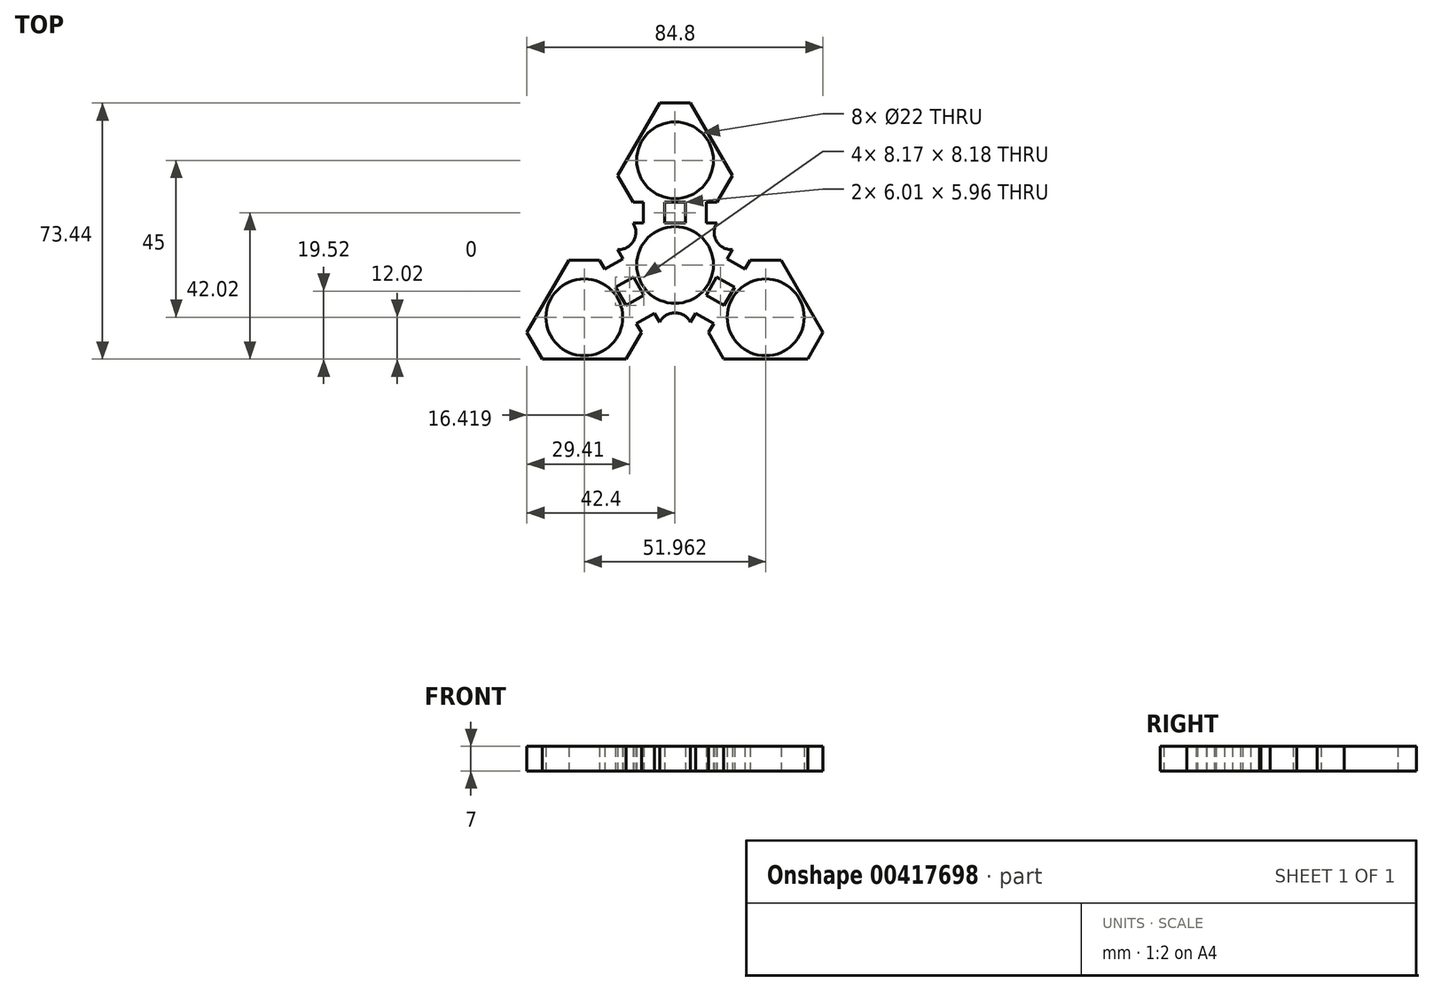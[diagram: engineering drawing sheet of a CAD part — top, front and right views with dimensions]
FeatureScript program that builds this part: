
annotation { "Feature Type Name" : "Feature", "Feature Type Description" : "" }
export const myFeature = defineFeature(function(context is Context, id is Id, definition is map)
    precondition{}
    {
        {
            var Q0;
            Q0=qCreatedBy(makeId("Top.planeOp"),FACE);
            var sketch = newSketch(context, id + "F0", { "sketchPlane" : qUnion([Q0])});
            skCircle(sketch, "E0", {"center": v(0, 0) * mm, "radius": 11 * mm});
            skLineSegment(sketch, "E1", {"start": v(0, 0) * mm, "end": v(0, 30) * mm});
            skCircle(sketch, "E2", {"center": v(0, 30) * mm, "radius": 11 * mm});
            skLineSegment(sketch, "E3.1.0", {"start": v(0, 0) * mm, "end": v(-25.98, -15) * mm});
            skCircle(sketch, "E3.1.1", {"center": v(-25.98, -15) * mm, "radius": 11 * mm});
            skLineSegment(sketch, "E3.2.0", {"start": v(0, 0) * mm, "end": v(25.98, -15) * mm});
            skCircle(sketch, "E3.2.1", {"center": v(25.98, -15) * mm, "radius": 11 * mm});
            skLineSegment(sketch, "E4", {"start": v(12.02, 12.02) * mm, "end": v(6.01, 12.02) * mm});
            skLineSegment(sketch, "E5.1.0", {"start": v(-16.42, 4.4) * mm, "end": v(-4.4, -16.42) * mm});
            skLineSegment(sketch, "E5.2.0", {"start": v(4.4, -16.42) * mm, "end": v(16.42, 4.4) * mm});
            skPoint(sketch, "E6", {"position": v(0, 15) * mm});
            skLineSegment(sketch, "E7.MirrorCS", {"start": v(12.02, 17.98) * mm, "end": v(0, 17.98) * mm});
            skLineSegment(sketch, "E8.MirrorCS", {"start": v(16.42, 25.6) * mm, "end": v(12.02, 17.98) * mm});
            skLineSegment(sketch, "E9.MirrorCS", {"start": v(4.4, 46.42) * mm, "end": v(16.42, 25.6) * mm});
            skLineSegment(sketch, "E10.MirrorCS", {"start": v(-4.4, 46.42) * mm, "end": v(4.4, 46.42) * mm});
            skLineSegment(sketch, "E11.MirrorCS", {"start": v(-16.42, 25.6) * mm, "end": v(-4.4, 46.42) * mm});
            skLineSegment(sketch, "E12.MirrorCS", {"start": v(-16.42, 25.6) * mm, "end": v(-12.02, 17.98) * mm});
            skLineSegment(sketch, "E13", {"start": v(0, 12.02) * mm, "end": v(-6.01, 12.02) * mm});
            skLineSegment(sketch, "E14", {"start": v(0, 17.98) * mm, "end": v(-12.02, 17.98) * mm});
            skPoint(sketch, "E15", {"position": v(-6.01, 12.02) * mm});
            skPoint(sketch, "E16", {"position": v(6.01, 12.02) * mm});
            skLineSegment(sketch, "E17", {"start": v(-6.01, 12.02) * mm, "end": v(-12.02, 12.02) * mm});
            skLineSegment(sketch, "E18", {"start": v(6.01, 12.02) * mm, "end": v(0, 12.02) * mm});
            skPoint(sketch, "E19", {"position": v(-3, 12.02) * mm});
            skPoint(sketch, "E20", {"position": v(-9.02, 12.02) * mm});
            skPoint(sketch, "E21", {"position": v(3, 12.02) * mm});
            skPoint(sketch, "E22", {"position": v(9.02, 12.02) * mm});
            skLineSegment(sketch, "E23", {"start": v(-3, 12.02) * mm, "end": v(-3, 17.98) * mm});
            skLineSegment(sketch, "E24", {"start": v(-9.02, 12.02) * mm, "end": v(-9.02, 17.98) * mm});
            skLineSegment(sketch, "E25.MirrorCS", {"start": v(3, 12.02) * mm, "end": v(3, 17.98) * mm});
            skLineSegment(sketch, "E26.MirrorCS", {"start": v(9.02, 12.02) * mm, "end": v(9.02, 17.98) * mm});
            skPoint(sketch, "E27", {"position": v(14.22, 8.21) * mm});
            skPoint(sketch, "E28", {"position": v(11.87, 6.86) * mm});
            skArc(sketch, "E29", {"start": v(12.02, 12.02) * mm, "mid": v(11.87, 6.86) * mm, "end": v(16.42, 4.4) * mm});
            skArc(sketch, "E30.1.0", {"start": v(-16.42, 4.4) * mm, "mid": v(-11.87, 6.86) * mm, "end": v(-12.02, 12.02) * mm});
            skArc(sketch, "E30.2.0", {"start": v(4.4, -16.42) * mm, "mid": v(0, -13.71) * mm, "end": v(-4.4, -16.42) * mm});
            skLineSegment(sketch, "E31.1.0", {"start": v(-14.92, 1.8) * mm, "end": v(-20.08, -1.18) * mm});
            skLineSegment(sketch, "E31.1.1", {"start": v(-11.91, -3.4) * mm, "end": v(-17.07, -6.39) * mm});
            skLineSegment(sketch, "E31.1.2", {"start": v(-8.9, -8.61) * mm, "end": v(-14.07, -11.6) * mm});
            skLineSegment(sketch, "E31.1.3", {"start": v(-5.9, -13.82) * mm, "end": v(-11.06, -16.8) * mm});
            skLineSegment(sketch, "E31.1.4", {"start": v(-15.57, -8.99) * mm, "end": v(-9.56, -19.4) * mm});
            skLineSegment(sketch, "E31.1.5", {"start": v(-21.58, 1.42) * mm, "end": v(-15.57, -8.99) * mm});
            skLineSegment(sketch, "E31.1.6", {"start": v(-30.38, 1.42) * mm, "end": v(-21.58, 1.42) * mm});
            skLineSegment(sketch, "E31.1.7", {"start": v(-42.4, -19.4) * mm, "end": v(-30.38, 1.42) * mm});
            skLineSegment(sketch, "E31.1.8", {"start": v(-38, -27.02) * mm, "end": v(-42.4, -19.4) * mm});
            skLineSegment(sketch, "E31.1.9", {"start": v(-13.96, -27.02) * mm, "end": v(-38, -27.02) * mm});
            skLineSegment(sketch, "E31.1.10", {"start": v(-13.96, -27.02) * mm, "end": v(-9.56, -19.4) * mm});
            skLineSegment(sketch, "E31.2.0", {"start": v(5.9, -13.82) * mm, "end": v(11.06, -16.8) * mm});
            skLineSegment(sketch, "E31.2.1", {"start": v(8.9, -8.61) * mm, "end": v(14.07, -11.6) * mm});
            skLineSegment(sketch, "E31.2.2", {"start": v(11.91, -3.4) * mm, "end": v(17.07, -6.39) * mm});
            skLineSegment(sketch, "E31.2.3", {"start": v(14.92, 1.8) * mm, "end": v(20.08, -1.18) * mm});
            skLineSegment(sketch, "E31.2.4", {"start": v(15.57, -8.99) * mm, "end": v(21.58, 1.42) * mm});
            skLineSegment(sketch, "E31.2.5", {"start": v(9.56, -19.4) * mm, "end": v(15.57, -8.99) * mm});
            skLineSegment(sketch, "E31.2.6", {"start": v(13.96, -27.02) * mm, "end": v(9.56, -19.4) * mm});
            skLineSegment(sketch, "E31.2.7", {"start": v(38, -27.02) * mm, "end": v(13.96, -27.02) * mm});
            skLineSegment(sketch, "E31.2.8", {"start": v(42.4, -19.4) * mm, "end": v(38, -27.02) * mm});
            skLineSegment(sketch, "E31.2.9", {"start": v(30.38, 1.42) * mm, "end": v(42.4, -19.4) * mm});
            skLineSegment(sketch, "E31.2.10", {"start": v(30.38, 1.42) * mm, "end": v(21.58, 1.42) * mm});
            skSolve(sketch);
        }
        {
            var Q0;
            Q0=makeQuery(id+"F0.imprint","IMPRINT",FACE,{"disambiguationData":[TD([[makeQuery(id+"F0.imprint","IMPRINT",EDGE,{"derivedFrom":sQuery(id+"F0.wireOp",EDGE,"E2")}),-1.0]])]});
            var Q1;
            {var subQ0=sQuery(id+"F0.wireOp",EDGE,"E23");Q1=makeQuery(id+"F0.imprint","IMPRINT",FACE,{"disambiguationData":[TD([[makeQuery(id+"F0.imprint","IMPRINT",EDGE,{"derivedFrom":subQ0}),1.0]])]});}
            var Q2;
            {var subQ0=sQuery(id+"F0.wireOp",EDGE,"E25.MirrorCS");Q2=makeQuery(id+"F0.imprint","IMPRINT",FACE,{"disambiguationData":[TD([[makeQuery(id+"F0.imprint","IMPRINT",EDGE,{"derivedFrom":subQ0}),-1.0]])]});}
            var Q3;
            {var subQ4=sQuery(id+"F0.wireOp",EDGE,"E29");Q3=makeQuery(id+"F0.imprint","IMPRINT",FACE,{"disambiguationData":[TD([[makeQuery(id+"F0.imprint","IMPRINT",EDGE,{"derivedFrom":subQ4}),-1.0]])]});}
            var Q4;
            {var subQ0=sQuery(id+"F0.wireOp",EDGE,"E30.1.0");Q4=makeQuery(id+"F0.imprint","IMPRINT",FACE,{"disambiguationData":[TD([[makeQuery(id+"F0.imprint","IMPRINT",EDGE,{"derivedFrom":subQ0}),-1.0]])]});}
            var Q5;
            {var subQ10=sQuery(id+"F0.wireOp",EDGE,"E30.2.0");Q5=makeQuery(id+"F0.imprint","IMPRINT",FACE,{"disambiguationData":[TD([[makeQuery(id+"F0.imprint","IMPRINT",EDGE,{"derivedFrom":subQ10}),-1.0]])]});}
            var Q6;
            {var subQ0=sQuery(id+"F0.wireOp",EDGE,"E31.1.2");Q6=makeQuery(id+"F0.imprint","IMPRINT",FACE,{"disambiguationData":[TD([[makeQuery(id+"F0.imprint","IMPRINT",EDGE,{"derivedFrom":subQ0}),1.0]])]});}
            var Q7;
            {var subQ0=sQuery(id+"F0.wireOp",EDGE,"E31.1.0");Q7=makeQuery(id+"F0.imprint","IMPRINT",FACE,{"disambiguationData":[TD([[makeQuery(id+"F0.imprint","IMPRINT",EDGE,{"derivedFrom":subQ0}),1.0]])]});}
            var Q8;
            Q8=makeQuery(id+"F0.imprint","IMPRINT",FACE,{"disambiguationData":[TD([[makeQuery(id+"F0.imprint","IMPRINT",EDGE,{"derivedFrom":sQuery(id+"F0.wireOp",EDGE,"E3.1.1")}),-1.0]])]});
            var Q9;
            {var subQ0=sQuery(id+"F0.wireOp",EDGE,"E31.2.2");Q9=makeQuery(id+"F0.imprint","IMPRINT",FACE,{"disambiguationData":[TD([[makeQuery(id+"F0.imprint","IMPRINT",EDGE,{"derivedFrom":subQ0}),1.0]])]});}
            var Q10;
            {var subQ0=sQuery(id+"F0.wireOp",EDGE,"E31.2.0");Q10=makeQuery(id+"F0.imprint","IMPRINT",FACE,{"disambiguationData":[TD([[makeQuery(id+"F0.imprint","IMPRINT",EDGE,{"derivedFrom":subQ0}),1.0]])]});}
            var Q11;
            Q11=makeQuery(id+"F0.imprint","IMPRINT",FACE,{"disambiguationData":[TD([[makeQuery(id+"F0.imprint","IMPRINT",EDGE,{"derivedFrom":sQuery(id+"F0.wireOp",EDGE,"E3.2.1")}),-1.0]])]});
            extrude(context, id + "F1", {"entities" : qUnion([Q0, Q1, Q2, Q3, Q4, Q5, Q6, Q7, Q8, Q9, Q10, Q11]), "endBound" : BoundingType.SYMMETRIC, "depth" : 7 * mm});
        }
    });
